FCSTD DOCUMENT  (FreeCAD 0.20R29177 +426 (Git))
Label: ASM_Stepper
License: All rights reserved
LicenseURL: http://en.wikipedia.org/wiki/All_rights_reserved
objects: App::Link×4, App::DocumentObjectGroup×3, PartDesign::CoordinateSystem×1, App::FeaturePython×1, App::Part×1
note: 1 computed .brp shape members not serialized (recipe doc carries the construction recipe); baked Part::Feature solids carry a one-line shape summary decoded from their .brp
EXTERNAL_REF file=Stepper17BracketFlat.FCStd obj=LCS_Mount
EXTERNAL_REF file=Stepper17BracketFlat.FCStd obj=Assembly
EXTERNAL_REF file=Stepper17.FCStd obj=LCS_mount
EXTERNAL_REF file=Stepper17BracketFlat.FCStd obj=LCS_Origin
EXTERNAL_REF file=Stepper17.FCStd obj=Body
EXTERNAL_REF file=FlangeHub5mm.FCStd obj=LCS_Origin
EXTERNAL_REF file=FlangeHub5mm.FCStd obj=Assembly
EXTERNAL_REF file=Wheel.FCStd obj=LCS_Origin
EXTERNAL_REF file=Wheel.FCStd obj=Assembly

FEATURE [App::DocumentObjectGroup] Parts
FEATURE [PartDesign::CoordinateSystem] LCS_Origin
  AttacherType = Attacher::AttachEngine3D
  MapMode = 2
  Support = -> [X_Axis]
FEATURE [App::DocumentObjectGroup] Constraints
FEATURE [App::FeaturePython] Variables  # WARN: FeaturePython — macro-defined, semantics opaque (R4)
  Type = App::PropertyContainer
FEATURE [App::DocumentObjectGroup] Configurations
FEATURE [App::Link] Stepper17BracketFlat
  AttachedBy = #LCS_Mount
  AttachedTo = Parent Assembly#LCS_Origin
  LinkPlacement = pos=(0,53.75,0) rot=(0,0,1;0rad)
  LinkedObject = -> <external Stepper17BracketFlat.FCStd>#Assembly
  Placement = pos=(0,53.75,0) rot=(0,0,1;0rad)
  SolverId = Asm4EE
  expr: Placement = LCS_Origin.Placement * AttachmentOffset * Stepper17BracketFlat#LCS_Mount.Placement ^ -1
FEATURE [App::Link] Stepper
  AttachedBy = #LCS_mount
  AttachedTo = Stepper17BracketFlat#LCS_Origin
  AttachmentOffset = pos=(0,0,0) rot=(0,1,0;3.14159rad)
  LinkPlacement = pos=(0,53.75,0) rot=(0,1,0;3.14159rad)
  LinkedObject = -> <external Stepper17.FCStd>#Body
  Placement = pos=(0,53.75,0) rot=(0,1,0;3.14159rad)
  SolverId = Asm4EE
  expr: Placement = Stepper17BracketFlat.Placement * Stepper17BracketFlat#LCS_Origin.Placement * AttachmentOffset * Stepper17#LCS_mount.Placement ^ -1
FEATURE [App::Link] FlangeHub5mm
  AttachedBy = #LCS_Origin
  AttachedTo = Stepper#LCS_mount
  AttachmentOffset = pos=(0,0,-14) rot=(1,0,0;3.14159rad)
  LinkPlacement = pos=(-1.7e-15,53.75,14) rot=(0,0,-1;3.14159rad)
  LinkedObject = -> <external FlangeHub5mm.FCStd>#Assembly
  Placement = pos=(-1.7e-15,53.75,14) rot=(0,0,-1;3.14159rad)
  SolverId = Asm4EE
  expr: Placement = Stepper.Placement * Stepper17#LCS_mount.Placement * AttachmentOffset * FlangeHub5mm#LCS_Origin.Placement ^ -1
FEATURE [App::Link] Wheel
  AttachedBy = #LCS_Origin
  AttachedTo = FlangeHub5mm#LCS_Origin
  AttachmentOffset = pos=(0,0,0) rot=(0,1,0;3.14159rad)
  LinkPlacement = pos=(-1.7e-15,53.75,14) rot=(1,0,0;3.14159rad)
  LinkedObject = -> <external Wheel.FCStd>#Assembly
  Placement = pos=(-1.7e-15,53.75,14) rot=(1,0,0;3.14159rad)
  SolverId = Asm4EE
  expr: Placement = FlangeHub5mm.Placement * FlangeHub5mm#LCS_Origin.Placement * AttachmentOffset * Wheel#LCS_Origin.Placement ^ -1
FEATURE [App::Part] Assembly
  AssemblyType = Part::Link
  Group = -> [LCS_Origin,Constraints,Variables,Configurations,Stepper17BracketFlat,Stepper,FlangeHub5mm,Wheel]
  Origin = -> Origin
  Type = Assembly

RESOLVED EXTERNAL PARTS (link-assembly join: the EXTERNAL_REF files above that resolve inside this repo's crawl, each included once):
---- part FlangeHub5mm.FCStd = doc fcstd_1ec9bd635127 ----
FCSTD DOCUMENT  (FreeCAD 0.20R29177 +426 (Git))
Label: FlangeHub5mm
License: All rights reserved
LicenseURL: http://en.wikipedia.org/wiki/All_rights_reserved
objects: Part::FeaturePython×4, App::DocumentObjectGroup×3, Sketcher::SketchObject×2, PartDesign::Revolution×1, PartDesign::Pocket×1, PartDesign::PolarPattern×1, PartDesign::Body×1, PartDesign::CoordinateSystem×1, App::FeaturePython×1, App::Part×1
note: 13 computed .brp shape members not serialized (recipe doc carries the construction recipe); baked Part::Feature solids carry a one-line shape summary decoded from their .brp

FEATURE [Sketcher::SketchObject] Sketch
  FullyConstrained = true
  MapMode = 5
  Placement = pos=(0,0,0) rot=(1,0,0;1.5708rad)
  Support = -> [XZ_Plane]
  sketch-geometry (6):
    g0: LineSegment StartX=2.51 StartY=12 StartZ=0 EndX=2.51 EndY=0 EndZ=0
    g1: LineSegment StartX=2.51 StartY=0 StartZ=0 EndX=13 EndY=0 EndZ=0
    g2: LineSegment StartX=13 StartY=0 StartZ=0 EndX=13 EndY=2 EndZ=0
    g3: LineSegment StartX=13 StartY=2 StartZ=0 EndX=6 EndY=2 EndZ=0
    g4: LineSegment StartX=6 StartY=2 StartZ=0 EndX=6 EndY=12 EndZ=0
    g5: LineSegment StartX=6 StartY=12 StartZ=0 EndX=2.51 EndY=12 EndZ=0
  constraints (18):
    c: Vertical(g0)
    c: Coincident(g1,g0)
    c: PointOnObject(g1,g-1)
    c: Horizontal(g1)
    c: Coincident(g2,g1)
    c: Coincident(g3,g2)
    c: Horizontal(g3)
    c: Coincident(g4,g3)
    c: Vertical(g4)
    c: Coincident(g5,g4)
    c: Coincident(g5,g0)
    c: Horizontal(g5)
    c: Vertical(g2)
    c: DistanceY(g2,g2) = 2
    c: DistanceX(g-1,g1) = 13
    c: DistanceX(g-1,g0) = 2.51
    c: DistanceY(g4,g4) = 10
    c: DistanceX(g-1,g4) = 6
FEATURE [PartDesign::Revolution] Revolution
  Angle = 360
  Axis = (0,-2e-16,1)
  Base = (0,0,0)
  Placement = pos=(0,0,0) rot=(1,0,0;1.5708rad)
  Profile = -> Sketch
  ReferenceAxis = -> Sketch [V_Axis]
  Reversed = true
FEATURE [Sketcher::SketchObject] Sketch001
  FullyConstrained = true
  MapMode = 5
  Support = -> [XY_Plane]
  sketch-geometry (1):
    g0: Circle CenterX=0 CenterY=9.5 CenterZ=0 NormalX=0 NormalY=0 NormalZ=1 AngleXU=0 Radius=1.6
  constraints (3):
    c: PointOnObject(g0,g-2)
    c: Diameter(g0) = 3.2
    c: DistanceY(g-1,g0) = 9.5
FEATURE [PartDesign::Pocket] Pocket  label="MountHole"
  BaseFeature = -> Revolution
  Direction = (0,0,-1)
  Length = 5
  Length2 = 5
  Placement = pos=(0,0,0) rot=(1,0,0;1.5708rad)
  Profile = -> Sketch001
  ReferenceAxis = -> Sketch001 [N_Axis]
  Reversed = true
  Type = 1
FEATURE [PartDesign::PolarPattern] PolarPattern
  Angle = 360
  Axis = -> Sketch001 [N_Axis]
  BaseFeature = -> Pocket
  Occurrences = 4
  Originals = -> [Pocket]
  Placement = pos=(0,0,0) rot=(1,0,0;1.5708rad)
FEATURE [PartDesign::Body] Body
  Group = -> [Sketch,Revolution,Sketch001,Pocket,PolarPattern]
  Origin = -> Origin
  Tip = -> PolarPattern
FEATURE [App::DocumentObjectGroup] Parts
FEATURE [PartDesign::CoordinateSystem] LCS_Origin
  AttacherType = Attacher::AttachEngine3D
  MapMode = 2
  Support = -> [X_Axis001]
FEATURE [App::FeaturePython] Variables  # WARN: FeaturePython — macro-defined, semantics opaque (R4)
  Type = App::PropertyContainer
FEATURE [App::DocumentObjectGroup] Constraints
FEATURE [App::DocumentObjectGroup] Configurations
FEATURE [Part::FeaturePython] Screw  label="M3x10-Screw"  # Fasteners workbench fastener (typed FeaturePython)
  Placement = pos=(9.5,-2.1e-15,2) rot=(0,0,1;0rad)
  baseObject = -> Body [Edge19]
  diameter = 4
  invert = true
  leftHanded = false
  length = 3
  lengthCustom = 10
  matchOuter = true
  offset = 0
  thread = false
  type = 34
FEATURE [Part::FeaturePython] Screw001  label="M3x10-Screw001"  # Fasteners workbench fastener (typed FeaturePython)
  Placement = pos=(-1.2e-15,-9.5,2) rot=(0,0,1;0rad)
  baseObject = -> PolarPattern [Edge21]
  diameter = 4
  invert = true
  leftHanded = false
  length = 3
  lengthCustom = 10
  matchOuter = true
  offset = 0
  thread = false
  type = 34
FEATURE [Part::FeaturePython] Screw002  label="M3x10-Screw002"  # Fasteners workbench fastener (typed FeaturePython)
  Placement = pos=(-9.5,1.9e-15,2) rot=(0,0,1;0rad)
  baseObject = -> PolarPattern [Edge17]
  diameter = 4
  invert = true
  leftHanded = false
  length = 3
  lengthCustom = 10
  matchOuter = true
  offset = 0
  thread = false
  type = 34
FEATURE [Part::FeaturePython] Screw003  label="M3x10-Screw003"  # Fasteners workbench fastener (typed FeaturePython)
  Placement = pos=(0,9.5,2) rot=(0,0,1;0rad)
  baseObject = -> PolarPattern [Edge15]
  diameter = 4
  invert = true
  leftHanded = false
  length = 3
  lengthCustom = 10
  matchOuter = true
  offset = 0
  thread = false
  type = 34
FEATURE [App::Part] Assembly
  AssemblyType = Part::Link
  Group = -> [LCS_Origin,Variables,Constraints,Configurations,Body,Screw,Screw001,Screw002,Screw003]
  Origin = -> Origin001
  Type = Assembly
---- part Stepper17.FCStd = doc fcstd_f327e92a600f ----
FCSTD DOCUMENT  (FreeCAD 0.20R29177 +426 (Git))
Label: Stepper17
License: All rights reserved
LicenseURL: http://en.wikipedia.org/wiki/All_rights_reserved
objects: Sketcher::SketchObject×5, PartDesign::Pad×3, PartDesign::Pocket×2, PartDesign::Chamfer×1, PartDesign::PolarPattern×1, PartDesign::CoordinateSystem×1, PartDesign::Body×1
note: 20 computed .brp shape members not serialized (recipe doc carries the construction recipe); baked Part::Feature solids carry a one-line shape summary decoded from their .brp

FEATURE [Sketcher::SketchObject] Sketch
  FullyConstrained = true
  MapMode = 5
  Support = -> [XY_Plane]
  sketch-geometry (4):
    g0: LineSegment StartX=-21 StartY=21 StartZ=0 EndX=21 EndY=21 EndZ=0
    g1: LineSegment StartX=21 StartY=21 StartZ=0 EndX=21 EndY=-21 EndZ=0
    g2: LineSegment StartX=21 StartY=-21 StartZ=0 EndX=-21 EndY=-21 EndZ=0
    g3: LineSegment StartX=-21 StartY=-21 StartZ=0 EndX=-21 EndY=21 EndZ=0
  constraints (11):
    c: Coincident(g0,g1)
    c: Coincident(g1,g2)
    c: Coincident(g2,g3)
    c: Coincident(g3,g0)
    c: Horizontal(g0)
    c: Horizontal(g2)
    c: Vertical(g1)
    c: Vertical(g3)
    c: Symmetric(g0,g2,g-1)
    c: Equal(g1,g0)
    c: DistanceX(g0,g0) = 42
FEATURE [PartDesign::Pad] Pad
  Direction = (1,1,1)
  Length = 48
  Length2 = 100
  Profile = -> Sketch
  Type = 0
FEATURE [PartDesign::Chamfer] Chamfer
  Angle = 45
  Base = -> Pad [Edge5,Edge8,Edge2,Edge1]
  BaseFeature = -> Pad
  ChamferType = 0
  FlipDirection = false
  Size = 4
  Size2 = 1
  SupportTransform = false
  UseAllEdges = false
FEATURE [Sketcher::SketchObject] Sketch001
  FullyConstrained = true
  MapMode = 5
  Support = -> [XY_Plane]
  sketch-geometry (1):
    g0: Circle CenterX=0 CenterY=0 CenterZ=0 NormalX=0 NormalY=0 NormalZ=1 AngleXU=0 Radius=11
  constraints (2):
    c: Coincident(g0,g-1)
    c: Diameter(g0) = 22
FEATURE [PartDesign::Pad] Pad001
  BaseFeature = -> Chamfer
  Direction = (1,1,1)
  Length = 2
  Length2 = 100
  Profile = -> Sketch001
  Reversed = true
  Type = 0
FEATURE [Sketcher::SketchObject] Sketch002
  FullyConstrained = true
  MapMode = 5
  Placement = pos=(0,0,-2) rot=(1,0,0;3.14159rad)
  Support = -> [Pad001]
  sketch-geometry (1):
    g0: Circle CenterX=0 CenterY=0 CenterZ=0 NormalX=0 NormalY=0 NormalZ=1 AngleXU=0 Radius=2.5
  constraints (2):
    c: Coincident(g0,g-1)
    c: Diameter(g0) = 5
FEATURE [PartDesign::Pad] Pad002
  BaseFeature = -> Pad001
  Direction = (1,1,1)
  Length = 24
  Length2 = 100
  Profile = -> Sketch002
  Type = 0
FEATURE [Sketcher::SketchObject] Sketch003
  ExternalGeometry = -> [Pad002]
  FullyConstrained = true
  MapMode = 5
  Placement = pos=(0,0,-26) rot=(1,0,0;3.14159rad)
  Support = -> [Pad002]
  sketch-geometry (2):
    g0: ArcOfCircle CenterX=0 CenterY=0 CenterZ=0 NormalX=0 NormalY=0 NormalZ=1 AngleXU=0 Radius=2.5 StartAngle=0.927295 EndAngle=2.2143
    g1: LineSegment StartX=-1.5 StartY=2 StartZ=0 EndX=1.5 EndY=2 EndZ=0
  constraints (6):
    c: Coincident(g0,g-1)
    c: PointOnObject(g0,g-3)
    c: Coincident(g1,g0)
    c: Coincident(g1,g0)
    c: DistanceY(g0,g0) = 2
    c: Horizontal(g1)
FEATURE [PartDesign::Pocket] Pocket
  BaseFeature = -> Pad002
  Direction = (1,1,1)
  Length = 15
  Length2 = 100
  Profile = -> Sketch003
  Type = 0
FEATURE [Sketcher::SketchObject] Sketch004
  FullyConstrained = true
  MapMode = 5
  Placement = pos=(0,0,0) rot=(1,0,0;3.14159rad)
  Support = -> [Pocket]
  sketch-geometry (4):
    g0: LineSegment StartX=0 StartY=0 StartZ=0 EndX=0 EndY=15.5 EndZ=0
    g1: LineSegment StartX=0 StartY=15.5 StartZ=0 EndX=15.5 EndY=15.5 EndZ=0
    g2: LineSegment StartX=15.5 StartY=15.5 StartZ=0 EndX=0 EndY=0 EndZ=0
    g3: Circle CenterX=15.5 CenterY=15.5 CenterZ=0 NormalX=0 NormalY=0 NormalZ=1 AngleXU=0 Radius=1.25
  constraints (10):
    c: Coincident(g0,g-1)
    c: PointOnObject(g0,g-2)
    c: Coincident(g1,g0)
    c: Horizontal(g1)
    c: Coincident(g2,g1)
    c: Coincident(g2,g-1)
    c: Equal(g0,g1)
    c: DistanceX(g1,g1) = 15.5
    c: Coincident(g3,g1)
    c: Diameter(g3) = 2.5
FEATURE [PartDesign::Pocket] Pocket001
  BaseFeature = -> Pocket
  Direction = (1,1,1)
  Length = 5
  Length2 = 100
  Profile = -> Sketch004
  Type = 0
FEATURE [PartDesign::PolarPattern] PolarPattern
  Angle = 360
  Axis = -> Z_Axis
  BaseFeature = -> Pocket001
  Occurrences = 4
  Originals = -> [Pocket001]
FEATURE [PartDesign::CoordinateSystem] LCS_mount
  AttacherType = Attacher::AttachEngine3D
  MapMode = 2
  Support = -> [XY_Plane]
FEATURE [PartDesign::Body] Body
  Group = -> [Sketch,Pad,Chamfer,Sketch001,Pad001,Sketch002,Pad002,Sketch003,Pocket,Sketch004,Pocket001,PolarPattern,LCS_mount]
  Origin = -> Origin
  Tip = -> PolarPattern
---- part Stepper17BracketFlat.FCStd = doc fcstd_d939f09d770a ----
FCSTD DOCUMENT  (FreeCAD 0.20R29177 +426 (Git))
Label: Stepper17BracketFlat
License: All rights reserved
LicenseURL: http://en.wikipedia.org/wiki/All_rights_reserved
objects: App::DocumentObjectGroup×3, PartDesign::CoordinateSystem×2, Sketcher::SketchObject×2, App::FeaturePython×1, PartDesign::Pad×1, PartDesign::Hole×1, PartDesign::Body×1, App::Part×1
note: 9 computed .brp shape members not serialized (recipe doc carries the construction recipe); baked Part::Feature solids carry a one-line shape summary decoded from their .brp

FEATURE [App::DocumentObjectGroup] Parts
FEATURE [PartDesign::CoordinateSystem] LCS_Origin
  AttacherType = Attacher::AttachEngine3D
  MapMode = 2
  Support = -> [X_Axis]
FEATURE [App::FeaturePython] Variables  # WARN: FeaturePython — macro-defined, semantics opaque (R4)
  Type = App::PropertyContainer
FEATURE [App::DocumentObjectGroup] Constraints
FEATURE [App::DocumentObjectGroup] Configurations
FEATURE [Sketcher::SketchObject] Sketch
  FullyConstrained = true
  MapMode = 5
  Support = -> [XY_Plane001]
  sketch-geometry (38):
    g0: Circle CenterX=0 CenterY=0 CenterZ=0 NormalX=0 NormalY=0 NormalZ=1 AngleXU=0 Radius=11.25
    g1: GeomPoint X=0 Y=-29 Z=0
    g2: ArcOfCircle CenterX=-15 CenterY=-39 CenterZ=0 NormalX=0 NormalY=0 NormalZ=1 AngleXU=0 Radius=2.15 StartAngle=0 EndAngle=3.14159
    g3: ArcOfCircle CenterX=-15 CenterY=-68.5 CenterZ=0 NormalX=0 NormalY=0 NormalZ=1 AngleXU=0 Radius=2.15 StartAngle=3.14159 EndAngle=6.28319
    g4: LineSegment StartX=-17.15 StartY=-39 StartZ=0 EndX=-17.15 EndY=-68.5 EndZ=0
    g5: LineSegment StartX=-12.85 StartY=-68.5 StartZ=0 EndX=-12.85 EndY=-39 EndZ=0
    g6: GeomPoint X=-15 Y=-36.85 Z=0
    g7: GeomPoint X=-15 Y=-70.65 Z=0
    g8: LineSegment StartX=-15 StartY=-36.85 StartZ=0 EndX=-15 EndY=-70.65 EndZ=0
    g9: ArcOfCircle CenterX=15 CenterY=-39 CenterZ=0 NormalX=0 NormalY=0 NormalZ=1 AngleXU=0 Radius=2.15 StartAngle=3.062e-13 EndAngle=3.14159
    g10: ArcOfCircle CenterX=15 CenterY=-68.5 CenterZ=0 NormalX=0 NormalY=0 NormalZ=1 AngleXU=0 Radius=2.15 StartAngle=3.14159 EndAngle=6.28319
    g11: LineSegment StartX=12.85 StartY=-39 StartZ=0 EndX=12.85 EndY=-68.5 EndZ=0
    g12: LineSegment StartX=17.15 StartY=-68.5 StartZ=0 EndX=17.15 EndY=-39 EndZ=0
    g13: GeomPoint X=15 Y=-36.85 Z=0
    g14: GeomPoint X=15 Y=-70.65 Z=0
    g15: LineSegment StartX=15 StartY=-36.85 StartZ=0 EndX=15 EndY=-70.65 EndZ=0
    g16: LineSegment StartX=-15 StartY=-39 StartZ=0 EndX=0 EndY=-39 EndZ=0
    g17: LineSegment StartX=0 StartY=-39 StartZ=0 EndX=15 EndY=-39 EndZ=0
    g18: LineSegment StartX=0 StartY=0 StartZ=0 EndX=15.5 EndY=15.5 EndZ=0
    g19: LineSegment StartX=15.5 StartY=15.5 StartZ=0 EndX=15.5 EndY=0 EndZ=0
    g20: Circle CenterX=15.5 CenterY=15.5 CenterZ=0 NormalX=0 NormalY=0 NormalZ=1 AngleXU=0 Radius=1.75
    g21: LineSegment StartX=25 StartY=21 StartZ=0 EndX=20.5 EndY=21 EndZ=0
    g22: LineSegment StartX=25 StartY=16.5 StartZ=0 EndX=25 EndY=21 EndZ=0
    g23: LineSegment StartX=-25 StartY=21 StartZ=0 EndX=-25 EndY=16.5 EndZ=0
    g24: LineSegment StartX=20.5 StartY=21 StartZ=0 EndX=-20.5 EndY=21 EndZ=0
    g25: LineSegment StartX=-20.5 StartY=21 StartZ=0 EndX=-25 EndY=21 EndZ=0
    g26: LineSegment StartX=-25 StartY=-79 StartZ=0 EndX=-20.5 EndY=-79 EndZ=0
    g27: LineSegment StartX=-25 StartY=16.5 StartZ=0 EndX=-25 EndY=-74.5 EndZ=0
    g28: LineSegment StartX=-25 StartY=-74.5 StartZ=0 EndX=-25 EndY=-79 EndZ=0
    g29: LineSegment StartX=-20.5 StartY=-79 StartZ=0 EndX=20.5 EndY=-79 EndZ=0
    g30: LineSegment StartX=20.5 StartY=-79 StartZ=0 EndX=25 EndY=-79 EndZ=0
    g31: LineSegment StartX=25 StartY=-79 StartZ=0 EndX=25 EndY=-74.5 EndZ=0
    g32: LineSegment StartX=25 StartY=-74.5 StartZ=0 EndX=25 EndY=16.5 EndZ=0
    g33: LineSegment StartX=-20.5 StartY=-79 StartZ=0 EndX=-25 EndY=-74.5 EndZ=0
    g34: LineSegment StartX=25 StartY=-74.5 StartZ=0 EndX=20.5 EndY=-79 EndZ=0
    g35: LineSegment StartX=25 StartY=16.5 StartZ=0 EndX=20.5 EndY=21 EndZ=0
    g36: LineSegment StartX=-25 StartY=16.5 StartZ=0 EndX=-20.5 EndY=21 EndZ=0
    g37: Circle CenterX=4.1e-15 CenterY=-53.75 CenterZ=0 NormalX=0 NormalY=0 NormalZ=1 AngleXU=0 Radius=5
  constraints (95):
    c: Coincident(g0,g-1)
    c: Diameter(g0) = 22.5
    c: Coincident(g22,g21)
    c: Coincident(g25,g23)
    c: Coincident(g28,g26)
    c: Coincident(g30,g31)
    c: Symmetric(g25,g31,g1)
    c: PointOnObject(g1,g-2)
    c: DistanceX(g25,g21) = 50
    c: DistanceY(g31,g22) = 100
    c: Tangent(g2,g4) = -1.5708
    c: Tangent(g4,g3) = -1.5708
    c: Tangent(g3,g5) = -1.5708
    c: Tangent(g5,g2) = -1.5708
    c: Equal(g2,g3)
    c: Vertical(g4)
    c: Diameter(g2) = 4.3
    c: PointOnObject(g6,g2)
    c: PointOnObject(g7,g3)
    c: Coincident(g8,g6)
    c: Coincident(g8,g7)
    c: Vertical(g8)
    c: PointOnObject(g3,g8)
    c: DistanceY(g8,g8) = 33.8
    c: Tangent(g9,g11) = -1.5708
    c: Tangent(g11,g10) = -1.5708
    c: Tangent(g10,g12) = -1.5708
    c: Tangent(g12,g9) = -1.5708
    c: Equal(g9,g10)
    c: Vertical(g11)
    c: Equal(g2,g9) = 4.3
    c: PointOnObject(g13,g9)
    c: PointOnObject(g14,g10)
    c: Coincident(g15,g13)
    c: Coincident(g15,g14)
    c: Vertical(g15)
    c: PointOnObject(g10,g15)
    c: Equal(g8,g15) = 33.8
    c: Coincident(g16,g2)
    c: PointOnObject(g16,g-2)
    c: Horizontal(g16)
    c: Coincident(g16,g17)
    c: Coincident(g17,g9)
    c: Horizontal(g17)
    c: Equal(g16,g17)
    c: DistanceX(g2,g9) = 30  'SlotSpacing'
    c: DistanceY(g28,g16) = 40
    c: Coincident(g18,g0)
    c: Angle(g-1,g18) = 0.785398
    c: Coincident(g19,g18)
    c: PointOnObject(g19,g-1)
    c: Vertical(g19)
    c: DistanceY(g19,g19) = 15.5
    c: Coincident(g20,g18)
    c: Diameter(g20) = 3.5
    c: DistanceY(g0,g25) = 21
    c: Coincident(g21,g24)
    c: Horizontal(g21)
    c: Coincident(g32,g22)
    c: Vertical(g22)
    c: Coincident(g23,g27)
    c: Vertical(g23)
    c: Coincident(g24,g25)
    c: Horizontal(g24)
    c: Horizontal(g25)
    c: Coincident(g26,g29)
    c: Horizontal(g26)
    c: Coincident(g27,g28)
    c: Vertical(g27)
    c: Vertical(g28)
    c: Coincident(g29,g30)
    c: Horizontal(g29)
    c: Horizontal(g30)
    c: Coincident(g31,g32)
    c: Vertical(g31)
    c: Vertical(g32)
    c: Equal(g31,g30)
    c: Equal(g30,g26)
    c: Equal(g26,g28)
    c: Equal(g28,g22)
    c: Equal(g22,g21)
    c: Equal(g21,g25)
    c: Equal(g25,g23)
    c: DistanceX(g25,g25) = 4.5
    c: Coincident(g33,g29)
    c: Coincident(g33,g27)
    c: Coincident(g34,g32)
    c: Coincident(g34,g29)
    c: Coincident(g35,g32)
    c: Coincident(g35,g24)
    c: Coincident(g36,g27)
    c: Coincident(g36,g24)
    c: Diameter(g37) = 10
    c: Symmetric(g3,g9,g37)
    c: DistanceY(g37,g0) = 53.75  'MountOffset'
FEATURE [PartDesign::Pad] Pad
  Direction = (0,0,1)
  Length = 3
  Length2 = 10
  Profile = -> Sketch
  ReferenceAxis = -> Sketch [N_Axis]
  Type = 0
FEATURE [Sketcher::SketchObject] Sketch001
  FullyConstrained = true
  MapMode = 5
  Support = -> [XY_Plane001]
  sketch-geometry (9):
    g0: LineSegment StartX=-15.5 StartY=-15.5 StartZ=0 EndX=-15.5 EndY=15.5 EndZ=0
    g1: LineSegment StartX=-15.5 StartY=15.5 StartZ=0 EndX=15.5 EndY=15.5 EndZ=0
    g2: LineSegment StartX=15.5 StartY=15.5 StartZ=0 EndX=15.5 EndY=-15.5 EndZ=0
    g3: LineSegment StartX=15.5 StartY=-15.5 StartZ=0 EndX=-15.5 EndY=-15.5 EndZ=0
    g4: GeomPoint X=0 Y=0 Z=0
    g5: Circle CenterX=-15.5 CenterY=15.5 CenterZ=0 NormalX=0 NormalY=0 NormalZ=1 AngleXU=0 Radius=1
    g6: Circle CenterX=15.5 CenterY=15.5 CenterZ=0 NormalX=0 NormalY=0 NormalZ=1 AngleXU=0 Radius=1
    g7: Circle CenterX=15.5 CenterY=-15.5 CenterZ=0 NormalX=0 NormalY=0 NormalZ=1 AngleXU=0 Radius=1
    g8: Circle CenterX=-15.5 CenterY=-15.5 CenterZ=0 NormalX=0 NormalY=0 NormalZ=1 AngleXU=0 Radius=1
  constraints (20):
    c: Coincident(g0,g1)
    c: Coincident(g1,g2)
    c: Coincident(g2,g3)
    c: Coincident(g3,g0)
    c: Horizontal(g1)
    c: Horizontal(g3)
    c: Vertical(g0)
    c: Vertical(g2)
    c: Symmetric(g1,g0,g4)
    c: Coincident(g4,g-1)
    c: DistanceY(g2,g2) = 31
    c: Equal(g2,g1)
    c: Coincident(g5,g0)
    c: Coincident(g6,g1)
    c: Coincident(g7,g2)
    c: Coincident(g8,g0)
    c: Equal(g8,g5)
    c: Equal(g5,g6)
    c: Equal(g6,g7)
    c: Diameter(g6) = 2
FEATURE [PartDesign::Hole] Hole
  BaseFeature = -> Pad
  CustomThreadClearance = 0
  Depth = 25
  DepthType = 0
  Diameter = 3.4
  DrillForDepth = false
  DrillPoint = 1
  DrillPointAngle = 118
  HoleCutCountersinkAngle = 90
  HoleCutCustomValues = false
  HoleCutDepth = 0
  HoleCutDiameter = 6.1
  HoleCutType = 0
  ModelThread = false
  Profile = -> Sketch001
  Reversed = true
  Tapered = false
  TaperedAngle = 90
  ThreadClass = 0
  ThreadDepth = 25
  ThreadDepthType = 0
  ThreadDirection = 0
  ThreadFit = 0
  ThreadSize = 9
  ThreadType = 1
  Threaded = false
  UseCustomThreadClearance = false
FEATURE [PartDesign::Body] Body
  Group = -> [Sketch,Pad,Sketch001,Hole]
  Origin = -> Origin001
  Tip = -> Hole
FEATURE [PartDesign::CoordinateSystem] LCS_Mount
  AttacherType = Attacher::AttachEngine3D
  AttachmentOffset = pos=(0,-53.75,0) rot=(0,0,1;0rad)
  MapMode = 2
  Placement = pos=(0,-53.75,0) rot=(0,0,1;0rad)
  Support = -> [LCS_Origin]
  expr: .AttachmentOffset.Base.y = <<Sketch>>.Constraints.MountOffset * -1
FEATURE [App::Part] Assembly
  AssemblyType = Part::Link
  Group = -> [LCS_Origin,Variables,Constraints,Configurations,Body,LCS_Mount]
  Origin = -> Origin
  Type = Assembly
---- part Wheel.FCStd = doc fcstd_3c4d531aaf43 ----
FCSTD DOCUMENT  (FreeCAD 0.20R29177 +426 (Git))
Label: Wheel
License: All rights reserved
LicenseURL: http://en.wikipedia.org/wiki/All_rights_reserved
objects: App::DocumentObjectGroup×3, PartDesign::CoordinateSystem×1, App::FeaturePython×1, Sketcher::SketchObject×1, PartDesign::Pad×1, PartDesign::Body×1, App::Part×1
note: 5 computed .brp shape members not serialized (recipe doc carries the construction recipe); baked Part::Feature solids carry a one-line shape summary decoded from their .brp

FEATURE [App::DocumentObjectGroup] Parts
FEATURE [PartDesign::CoordinateSystem] LCS_Origin
  AttacherType = Attacher::AttachEngine3D
  MapMode = 2
  Support = -> [X_Axis]
FEATURE [App::DocumentObjectGroup] Constraints
FEATURE [App::FeaturePython] Variables  # WARN: FeaturePython — macro-defined, semantics opaque (R4)
  Type = App::PropertyContainer
FEATURE [App::DocumentObjectGroup] Configurations
FEATURE [Sketcher::SketchObject] Sketch
  FullyConstrained = true
  MapMode = 5
  Support = -> [XY_Plane001]
  sketch-geometry (2):
    g0: Circle CenterX=0 CenterY=0 CenterZ=0 NormalX=0 NormalY=0 NormalZ=1 AngleXU=0 Radius=60
    g1: Circle CenterX=0 CenterY=0 CenterZ=0 NormalX=0 NormalY=0 NormalZ=1 AngleXU=0 Radius=2.5
  constraints (4):
    c: Coincident(g0,g-1)
    c: Diameter(g0) = 120
    c: Coincident(g1,g0)
    c: Diameter(g1) = 5
FEATURE [PartDesign::Pad] Pad
  Direction = (0,0,1)
  Length = 6.35
  Length2 = 10
  Profile = -> Sketch
  ReferenceAxis = -> Sketch [N_Axis]
  Type = 0
FEATURE [PartDesign::Body] Body
  Group = -> [Sketch,Pad]
  Origin = -> Origin001
  Tip = -> Pad
FEATURE [App::Part] Assembly
  AssemblyType = Part::Link
  Group = -> [LCS_Origin,Constraints,Variables,Configurations,Body]
  Origin = -> Origin
  Type = Assembly
